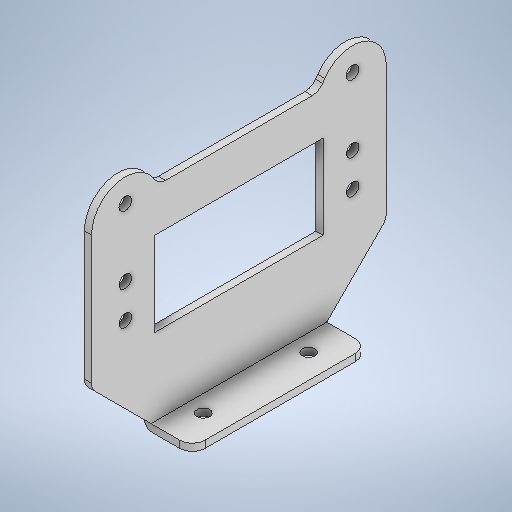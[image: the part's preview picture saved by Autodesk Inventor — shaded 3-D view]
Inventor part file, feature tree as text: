
AUTODESK INVENTOR PART (.ipt)
format: ipt  version: 2025.2 (Build 292293000, 293)  size: 347,136 bytes
history: native  units: mm
features: extrude x4, fillet x4, sketch x4
ambient origin geometry x8: Origin, YZ Plane, XZ Plane, XY Plane, X Axis, Y Axis, Z Axis, Center Point
bodies: Solid1 (feature_tree)
feature tree (12):
  extrude  "Extrusion1"  Depth=3.0mm
  extrude  "Extrusion2"  Depth=3.0mm
  extrude  "Extrusion3"  Depth=40.0mm
  fillet  "Fillet1"  Radius=20.0mm
  fillet  "Fillet2"  Radius=30.0mm
  fillet  "Fillet3"  Radius=3.0mm
  fillet  "Fillet4"  Radius=3.0mm
  extrude  "Extrusion4"  Depth=50.0mm
  sketch  "Sketch1"  dims[d0=12.5mm d1=3.0mm]
  sketch  "Sketch2"  dims[d2=3.0mm d3=3.0mm]
  sketch  "Sketch3"  dims[d4=1.7mm d5=0.0mm d6=40.0mm d7=20.0mm d8=30.0mm d9=3.0mm d10=3.0mm]
  sketch  "Sketch4"  dims[d11=50.0mm d12=50.0mm d13=54.0mm d14=27.0mm d15=20.0mm d16=45.0deg d17=40.0mm d18=90.0deg d19=20.0mm d20=135.0deg d21=40.0mm d22=1.7mm d23=0.0mm d24=10.0mm d25=4.0mm d26=4.0mm d27=4.0mm d28=4.0mm d29=10.0mm d30=0.0mm d31=8.0mm d32=3.0mm d33=3.0mm d34=2.0mm d35=54.0mm d36=8.0mm d37=6.0mm d38=7.0mm d39=3.0mm d40=3.0mm d41=3.0mm d42=3.0mm d43=10.0mm d44=0.0mm]
